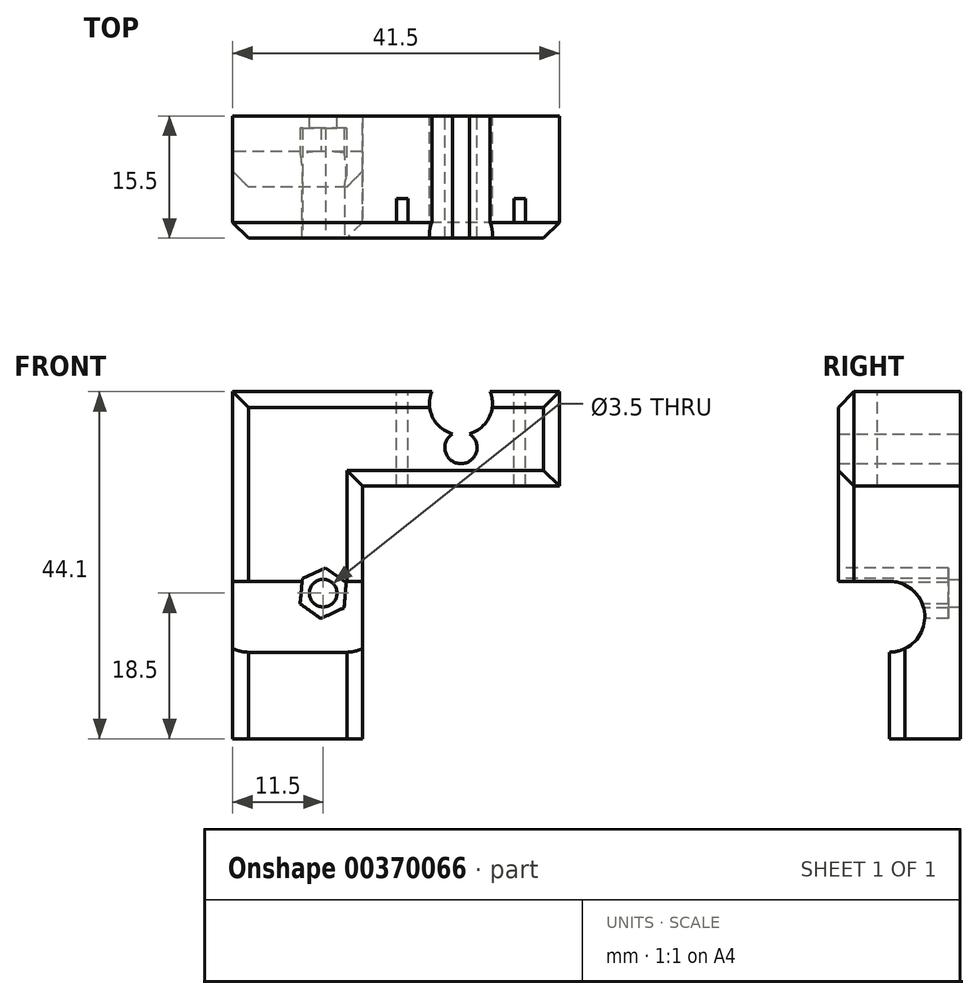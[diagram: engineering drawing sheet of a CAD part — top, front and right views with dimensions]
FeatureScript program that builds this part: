
annotation { "Feature Type Name" : "Feature", "Feature Type Description" : "" }
export const myFeature = defineFeature(function(context is Context, id is Id, definition is map)
    precondition{}
    {
        {
            var Q0;
            Q0=qCreatedBy(makeId("Front.planeOp"),FACE);
            var sketch = newSketch(context, id + "F0", { "sketchPlane" : qUnion([Q0])});
            skLineSegment(sketch, "E0.right", {"start": v(16.5, 21.37) * mm, "end": v(16.5, 38.5) * mm});
            skPoint(sketch, "E1.centerSnap0", {"position": v(8.25, 38.5) * mm});
            skLineSegment(sketch, "E2.trimOffspring", {"start": v(10.09, 38.5) * mm, "end": v(10.09, 38.5) * mm});
            skLineSegment(sketch, "E3", {"start": v(0, 38.5) * mm, "end": v(0, 21.37) * mm});
            skPoint(sketch, "E4.start.orphan", {"position": v(8.25, 33.37) * mm});
            skPoint(sketch, "E5.center.orphan", {"position": v(8.25, 37) * mm});
            skPoint(sketch, "E6.end.orphan", {"position": v(8.25, 21.37) * mm});
            skLineSegment(sketch, "E7", {"start": v(0, 38.5) * mm, "end": v(4.54, 38.5) * mm});
            skArc(sketch, "E8", {"start": v(4.54, 38.5) * mm, "mid": v(4.65, 35.25) * mm, "end": v(7.13, 33.16) * mm});
            skLineSegment(sketch, "E9.trimOffspring", {"start": v(11.96, 38.5) * mm, "end": v(16.5, 38.5) * mm});
            skArc(sketch, "E10", {"start": v(7.13, 33.16) * mm, "mid": v(8.25, 29.4) * mm, "end": v(9.37, 33.16) * mm});
            skArc(sketch, "E11.trimOffspring", {"start": v(9.37, 33.16) * mm, "mid": v(11.85, 35.25) * mm, "end": v(11.96, 38.5) * mm});
            skLineSegment(sketch, "E12", {"start": v(8.25, 21) * mm, "end": v(16.5, 21) * mm});
            skLineSegment(sketch, "E13", {"start": v(16.5, 21) * mm, "end": v(16.5, 21.37) * mm});
            skLineSegment(sketch, "E14", {"start": v(8.25, 21) * mm, "end": v(0, 21) * mm});
            skLineSegment(sketch, "E15", {"start": v(0, 21) * mm, "end": v(0, 21.37) * mm});
            skSolve(sketch);
        }
        {
            var Q0;
            Q0 = qSketchRegion(id + "F0", true);
            extrude(context, id + "F1", {"entities" : qUnion([Q0]), "depth" : 17.5 * mm});
        }
        {
            var Q0;
            Q0=makeQuery(id+"F1.opExtrude","CAP_FACE",FACE,{"disambiguationData":[OSD([sQuery(id+"F0.wireOp",EDGE,"E0.right"),sQuery(id+"F0.wireOp",EDGE,"E3"),sQuery(id+"F0.wireOp",EDGE,"E7"),sQuery(id+"F0.wireOp",EDGE,"E8"),sQuery(id+"F0.wireOp",EDGE,"E9.trimOffspring"),sQuery(id+"F0.wireOp",EDGE,"E10"),sQuery(id+"F0.wireOp",EDGE,"E11.trimOffspring"),sQuery(id+"F0.wireOp",EDGE,"E12"),sQuery(id+"F0.wireOp",EDGE,"E13"),sQuery(id+"F0.wireOp",EDGE,"E14"),sQuery(id+"F0.wireOp",EDGE,"E15")])],"isStart":true});
            var sketch = newSketch(context, id + "F2", { "sketchPlane" : qUnion([Q0])});
            skLineSegment(sketch, "E16.bottom", {"start": v(-16.5, 21) * mm, "end": v(0, 21) * mm});
            skLineSegment(sketch, "E16.top", {"start": v(-16.5, 1) * mm, "end": v(0, 1) * mm});
            skLineSegment(sketch, "E16.left", {"start": v(-16.5, 21) * mm, "end": v(-16.5, 1) * mm});
            skLineSegment(sketch, "E16.right", {"start": v(0, 21) * mm, "end": v(0, 1) * mm});
            skSolve(sketch);
        }
        {
            var Q0;
            Q0=makeQuery(id+"F2.imprint","IMPRINT",FACE,{"disambiguationData":[TD([[makeQuery(id+"F2.imprint","IMPRINT",EDGE,{"derivedFrom":sQuery(id+"F2.wireOp",EDGE,"E16.bottom")}),-1.0]])]});
            extrude(context, id + "F3", {"entities" : qUnion([Q0]), "operationType" : NewBodyOperationType.ADD, "oppositeDirection" : true, "depth" : 11 * mm});
        }
        {
            var Q0;
            Q0=makeQuery(id+"F3.boolean.opBoolean","MERGE",FACE,{"derivedFrom":[makeQuery(id+"F1.opExtrude","CAP_FACE",FACE,{"disambiguationData":[OSD([sQuery(id+"F0.wireOp",EDGE,"E0.right"),sQuery(id+"F0.wireOp",EDGE,"E3"),sQuery(id+"F0.wireOp",EDGE,"E7"),sQuery(id+"F0.wireOp",EDGE,"E8"),sQuery(id+"F0.wireOp",EDGE,"E9.trimOffspring"),sQuery(id+"F0.wireOp",EDGE,"E10"),sQuery(id+"F0.wireOp",EDGE,"E11.trimOffspring"),sQuery(id+"F0.wireOp",EDGE,"E12"),sQuery(id+"F0.wireOp",EDGE,"E13"),sQuery(id+"F0.wireOp",EDGE,"E14"),sQuery(id+"F0.wireOp",EDGE,"E15")])],"isStart":true}),makeQuery(id+"F3.opExtrude","CAP_FACE",FACE,{"disambiguationData":[OSD([sQuery(id+"F2.wireOp",EDGE,"E16.bottom"),sQuery(id+"F2.wireOp",EDGE,"E16.top"),sQuery(id+"F2.wireOp",EDGE,"E16.left"),sQuery(id+"F2.wireOp",EDGE,"E16.right")])],"isStart":true})]});
            var sketch = newSketch(context, id + "F4", { "sketchPlane" : qUnion([Q0])});
            skPoint(sketch, "E17.endSnap0", {"position": v(-8.25, 29.4) * mm});
            skCircle(sketch, "E18", {"center": v(-11.5, 19.5) * mm, "radius": 1.75 * mm});
            skPoint(sketch, "E19.orphan", {"position": v(-16.5, 19.5) * mm});
            skPoint(sketch, "E20.end.orphan", {"position": v(-8.25, 19.5) * mm});
            skSolve(sketch);
        }
        {
            var Q0;
            Q0=makeQuery(id+"F3.boolean.opBoolean","MERGE",FACE,{"derivedFrom":[makeQuery(id+"F1.opExtrude","SWEPT_FACE",FACE,{"disambiguationData":[OSD([sQuery(id+"F0.wireOp",EDGE,"E3"),sQuery(id+"F0.wireOp",EDGE,"E15")])]}),makeQuery(id+"F3.opExtrude","SWEPT_FACE",FACE,{"disambiguationData":[OSD([sQuery(id+"F2.wireOp",EDGE,"E16.right")])]})]});
            var sketch = newSketch(context, id + "F5", { "sketchPlane" : qUnion([Q0])});
            skLineSegment(sketch, "E21", {"start": v(11, 21) * mm, "end": v(11, 16.5) * mm});
            skArc(sketch, "E22", {"start": v(11, 21) * mm, "mid": v(6.5, 16.5) * mm, "end": v(11, 12) * mm});
            skLineSegment(sketch, "E23", {"start": v(11, 16.5) * mm, "end": v(11, 12) * mm});
            skPoint(sketch, "E24.orphan", {"position": v(11, 11) * mm});
            skSolve(sketch);
        }
        {
            var Q0;
            Q0 = qSketchRegion(id + "F4", true);
            extrude(context, id + "F6", {"entities" : qUnion([Q0]), "operationType" : NewBodyOperationType.REMOVE, "oppositeDirection" : true, "depth" : 22.5 * mm});
        }
        {
            var Q0;
            Q0=makeQuery(id+"F3.opExtrude","CAP_FACE",FACE,{"disambiguationData":[OSD([sQuery(id+"F2.wireOp",EDGE,"E16.bottom"),sQuery(id+"F2.wireOp",EDGE,"E16.top"),sQuery(id+"F2.wireOp",EDGE,"E16.left"),sQuery(id+"F2.wireOp",EDGE,"E16.right")])],"isStart":false});
            var sketch = newSketch(context, id + "F7", { "sketchPlane" : qUnion([Q0])});
            skCircle(sketch, "E25.cCircle", {"center": v(11.5, 19.5) * mm, "radius": 2.8 * mm, "construction": true});
            skLineSegment(sketch, "E25.0", {"start": v(14.43, 20.86) * mm, "end": v(14.14, 17.64) * mm});
            skLineSegment(sketch, "E25.1", {"start": v(14.14, 17.64) * mm, "end": v(11.2, 16.28) * mm});
            skLineSegment(sketch, "E25.2", {"start": v(11.2, 16.28) * mm, "end": v(8.57, 18.14) * mm});
            skLineSegment(sketch, "E25.3", {"start": v(8.57, 18.14) * mm, "end": v(8.86, 21.36) * mm});
            skLineSegment(sketch, "E25.4", {"start": v(8.86, 21.36) * mm, "end": v(11.8, 22.72) * mm});
            skLineSegment(sketch, "E25.5", {"start": v(11.8, 22.72) * mm, "end": v(14.43, 20.86) * mm});
            skPoint(sketch, "E25.0.midPoint", {"position": v(14.29, 19.25) * mm});
            skSolve(sketch);
        }
        {
            var Q0;
            Q0 = qSketchRegion(id + "F7", true);
            extrude(context, id + "F8", {"entities" : qUnion([Q0]), "operationType" : NewBodyOperationType.REMOVE, "oppositeDirection" : true, "depth" : 7.5 * mm});
        }
        {
            var Q0;
            Q0 = qSketchRegion(id + "F7", true);
            extrude(context, id + "F9", {"entities" : qUnion([Q0]), "operationType" : NewBodyOperationType.REMOVE, "depth" : 13.1 * mm});
        }
        {
            var Q0;
            Q0 = qSketchRegion(id + "F5", true);
            extrude(context, id + "F10", {"entities" : qUnion([Q0]), "operationType" : NewBodyOperationType.REMOVE, "oppositeDirection" : true, "depth" : 24.9 * mm});
        }
        {
            var Q0;
            Q0=makeQuery(id+"F3.boolean.opBoolean","MERGE",FACE,{"derivedFrom":[makeQuery(id+"F1.opExtrude","CAP_FACE",FACE,{"disambiguationData":[OSD([sQuery(id+"F0.wireOp",EDGE,"E0.right"),sQuery(id+"F0.wireOp",EDGE,"E3"),sQuery(id+"F0.wireOp",EDGE,"E7"),sQuery(id+"F0.wireOp",EDGE,"E8"),sQuery(id+"F0.wireOp",EDGE,"E9.trimOffspring"),sQuery(id+"F0.wireOp",EDGE,"E10"),sQuery(id+"F0.wireOp",EDGE,"E11.trimOffspring"),sQuery(id+"F0.wireOp",EDGE,"E12"),sQuery(id+"F0.wireOp",EDGE,"E13"),sQuery(id+"F0.wireOp",EDGE,"E14"),sQuery(id+"F0.wireOp",EDGE,"E15")])],"isStart":true}),makeQuery(id+"F3.opExtrude","CAP_FACE",FACE,{"disambiguationData":[OSD([sQuery(id+"F2.wireOp",EDGE,"E16.bottom"),sQuery(id+"F2.wireOp",EDGE,"E16.top"),sQuery(id+"F2.wireOp",EDGE,"E16.left"),sQuery(id+"F2.wireOp",EDGE,"E16.right")])],"isStart":true})]});
            var sketch = newSketch(context, id + "F11", { "sketchPlane" : qUnion([Q0])});
            skLineSegment(sketch, "E26", {"start": v(-16.5, 38.5) * mm, "end": v(-16.5, 1) * mm});
            skLineSegment(sketch, "E27", {"start": v(-16.5, 1) * mm, "end": v(0, 1) * mm});
            skLineSegment(sketch, "E28", {"start": v(0, 1) * mm, "end": v(0, 38.5) * mm});
            skLineSegment(sketch, "E29", {"start": v(0, 38.5) * mm, "end": v(-4.54, 38.5) * mm});
            skLineSegment(sketch, "E30", {"start": v(-11.96, 38.5) * mm, "end": v(-16.5, 38.5) * mm});
            skArc(sketch, "E31", {"start": v(-11.96, 38.5) * mm, "mid": v(-11.85, 35.25) * mm, "end": v(-9.37, 33.16) * mm});
            skArc(sketch, "E32", {"start": v(-9.37, 33.16) * mm, "mid": v(-8.25, 29.4) * mm, "end": v(-7.13, 33.16) * mm});
            skArc(sketch, "E33.trimOffspring", {"start": v(-7.13, 33.16) * mm, "mid": v(-4.65, 35.25) * mm, "end": v(-4.54, 38.5) * mm});
            skSolve(sketch);
        }
        {
            var Q0;
            Q0=makeQuery(id+"F11.imprint","IMPRINT",FACE,{"disambiguationData":[TD([[makeQuery(id+"F11.imprint","IMPRINT",EDGE,{"derivedFrom":sQuery(id+"F11.wireOp",EDGE,"E26")}),-1.0]])]});
            extrude(context, id + "F12", {"entities" : qUnion([Q0]), "operationType" : NewBodyOperationType.REMOVE, "oppositeDirection" : true, "depth" : 2 * mm});
        }
        {
            var Q0;
            Q0=makeQuery(id+"F3.boolean.opBoolean","MERGE",FACE,{"derivedFrom":[makeQuery(id+"F1.opExtrude","SWEPT_FACE",FACE,{"disambiguationData":[OSD([sQuery(id+"F0.wireOp",EDGE,"E0.right"),sQuery(id+"F0.wireOp",EDGE,"E13")])]}),makeQuery(id+"F3.opExtrude","SWEPT_FACE",FACE,{"disambiguationData":[OSD([sQuery(id+"F2.wireOp",EDGE,"E16.left")])]})]});
            var sketch = newSketch(context, id + "F13", { "sketchPlane" : qUnion([Q0])});
            skLineSegment(sketch, "E34.top", {"start": v(-2, 33.1) * mm, "end": v(-17.5, 33.1) * mm});
            skLineSegment(sketch, "E34.left", {"start": v(-2, 38.5) * mm, "end": v(-2, 33.1) * mm});
            skLineSegment(sketch, "E34.right", {"start": v(-17.5, 38.5) * mm, "end": v(-17.5, 33.1) * mm});
            skLineSegment(sketch, "E35.top", {"start": v(-2, 45.1) * mm, "end": v(-17.5, 45.1) * mm});
            skLineSegment(sketch, "E35.left", {"start": v(-2, 38.5) * mm, "end": v(-2, 45.1) * mm});
            skLineSegment(sketch, "E35.right", {"start": v(-17.5, 38.5) * mm, "end": v(-17.5, 45.1) * mm});
            skSolve(sketch);
        }
        {
            var Q0;
            Q0=makeQuery(id+"F13.imprint","IMPRINT",FACE,{"disambiguationData":[TD([[makeQuery(id+"F13.imprint","IMPRINT",EDGE,{"derivedFrom":sQuery(id+"F13.wireOp",EDGE,"E35.top")}),1.0]])]});
            var Q1;
            Q1=makeQuery(id+"F13.imprint","IMPRINT",FACE,{"disambiguationData":[TD([[makeQuery(id+"F13.imprint","IMPRINT",EDGE,{"derivedFrom":sQuery(id+"F13.wireOp",EDGE,"E34.top")}),-1.0]])]});
            extrude(context, id + "F14", {"entities" : qUnion([Q0, Q1]), "operationType" : NewBodyOperationType.ADD, "depth" : 25 * mm});
        }
        {
            var Q0;
            Q0=makeQuery(id+"F14.opExtrude","CAP_FACE",FACE,{"disambiguationData":[OSD([sQuery(id+"F13.wireOp",EDGE,"E34.top"),sQuery(id+"F13.wireOp",EDGE,"E34.left"),sQuery(id+"F13.wireOp",EDGE,"E34.right"),sQuery(id+"F13.wireOp",EDGE,"E35.top"),sQuery(id+"F13.wireOp",EDGE,"E35.left"),sQuery(id+"F13.wireOp",EDGE,"E35.right")])],"isStart":true});
            extrude(context, id + "F15", {"entities" : qUnion([Q0]), "operationType" : NewBodyOperationType.ADD, "depth" : 16.5 * mm});
        }
        {
            var Q0;
            {var subQ0=sQuery(id+"F13.wireOp",EDGE,"E35.left");var subQ1=sQuery(id+"F13.wireOp",EDGE,"E34.left");Q0=makeQuery(id+"F15.boolean.opBoolean","MERGE",FACE,{"derivedFrom":[makeQuery(id+"F14.boolean.opBoolean","MERGE",FACE,{"derivedFrom":[makeQuery(id+"F12.boolean.opBoolean","COPY",FACE,{"derivedFrom":makeQuery(id+"F12.opExtrude","CAP_FACE",FACE,{"disambiguationData":[OSD([sQuery(id+"F4.wireOp",EDGE,"E18"),sQuery(id+"F11.wireOp",EDGE,"E26"),sQuery(id+"F11.wireOp",EDGE,"E27"),sQuery(id+"F11.wireOp",EDGE,"E28"),sQuery(id+"F11.wireOp",EDGE,"E29"),sQuery(id+"F11.wireOp",EDGE,"E30"),sQuery(id+"F11.wireOp",EDGE,"E31"),sQuery(id+"F11.wireOp",EDGE,"E32"),sQuery(id+"F11.wireOp",EDGE,"E33.trimOffspring")])],"isStart":false})}),makeQuery(id+"F14.opExtrude","SWEPT_FACE",FACE,{"disambiguationData":[OSD([subQ1,subQ0])]})]}),makeQuery(id+"F15.opExtrude","SWEPT_FACE",FACE,{"disambiguationData":[OSD([subQ1,subQ0])]})]});}
            var sketch = newSketch(context, id + "F16", { "sketchPlane" : qUnion([Q0])});
            skPoint(sketch, "E36.endSnap0", {"position": v(-29, 45.1) * mm});
            skArc(sketch, "E37", {"start": v(-27.93, 39.74) * mm, "mid": v(-25.4, 41.83) * mm, "end": v(-25.3, 45.1) * mm});
            skPoint(sketch, "E36.start.orphan", {"position": v(-29, 45.1) * mm});
            skArc(sketch, "E38", {"start": v(-30.07, 39.74) * mm, "mid": v(-29, 35.94) * mm, "end": v(-27.93, 39.74) * mm});
            skArc(sketch, "E39.trimOffspring", {"start": v(-32.7, 45.1) * mm, "mid": v(-32.6, 41.83) * mm, "end": v(-30.07, 39.74) * mm});
            skPoint(sketch, "E40.trimOffspring.end.orphan", {"position": v(-41.5, 45.1) * mm});
            skPoint(sketch, "E41.start.orphan", {"position": v(-16.5, 45.1) * mm});
            skLineSegment(sketch, "E42", {"start": v(-32.7, 45.1) * mm, "end": v(-25.3, 45.1) * mm});
            skSolve(sketch);
        }
        {
            var Q0;
            Q0 = qSketchRegion(id + "F16", true);
            extrude(context, id + "F17", {"entities" : qUnion([Q0]), "operationType" : NewBodyOperationType.REMOVE, "oppositeDirection" : true, "depth" : 25 * mm});
        }
        {
            var Q0;
            {var subQ6=sQuery(id+"F13.wireOp",EDGE,"E35.top");Q0=makeQuery(id+"F17.boolean.opBoolean","SPLIT",FACE,{"disambiguationData":[TD([makeQuery(id+"F3.opExtrude","SWEPT_FACE",FACE,{"disambiguationData":[OSD([sQuery(id+"F2.wireOp",EDGE,"E16.right")])]})])],"derivedFrom":makeQuery(id+"F15.boolean.opBoolean","MERGE",FACE,{"derivedFrom":[makeQuery(id+"F14.opExtrude","SWEPT_FACE",FACE,{"disambiguationData":[OSD([subQ6])]}),makeQuery(id+"F15.opExtrude","SWEPT_FACE",FACE,{"disambiguationData":[OSD([subQ6])]})]})});}
            var sketch = newSketch(context, id + "F18", { "sketchPlane" : qUnion([Q0])});
            skLineSegment(sketch, "E43.bottom", {"start": v(20.8, -12.5) * mm, "end": v(22.3, -12.5) * mm});
            skLineSegment(sketch, "E43.top", {"start": v(20.8, -15.5) * mm, "end": v(22.3, -15.5) * mm});
            skLineSegment(sketch, "E43.left", {"start": v(20.8, -12.5) * mm, "end": v(20.8, -15.5) * mm});
            skLineSegment(sketch, "E43.right", {"start": v(22.3, -12.5) * mm, "end": v(22.3, -15.5) * mm});
            skLineSegment(sketch, "E44.bottom", {"start": v(35.7, -12.5) * mm, "end": v(37.2, -12.5) * mm});
            skLineSegment(sketch, "E44.top", {"start": v(35.7, -15.5) * mm, "end": v(37.2, -15.5) * mm});
            skLineSegment(sketch, "E44.left", {"start": v(35.7, -12.5) * mm, "end": v(35.7, -15.5) * mm});
            skLineSegment(sketch, "E44.right", {"start": v(37.2, -12.5) * mm, "end": v(37.2, -15.5) * mm});
            skSolve(sketch);
        }
        {
            var Q0;
            Q0 = qSketchRegion(id + "F18", true);
            extrude(context, id + "F19", {"entities" : qUnion([Q0]), "operationType" : NewBodyOperationType.REMOVE, "oppositeDirection" : true, "depth" : 25 * mm});
        }
        {
            var Q0;
            {var subQ0=sQuery(id+"F13.wireOp",EDGE,"E35.right");var subQ1=sQuery(id+"F13.wireOp",EDGE,"E34.right");Q0=makeQuery(id+"F15.boolean.opBoolean","MERGE",FACE,{"derivedFrom":[makeQuery(id+"F14.boolean.opBoolean","MERGE",FACE,{"derivedFrom":[makeQuery(id+"F1.opExtrude","CAP_FACE",FACE,{"disambiguationData":[OSD([sQuery(id+"F0.wireOp",EDGE,"E0.right"),sQuery(id+"F0.wireOp",EDGE,"E3"),sQuery(id+"F0.wireOp",EDGE,"E7"),sQuery(id+"F0.wireOp",EDGE,"E8"),sQuery(id+"F0.wireOp",EDGE,"E9.trimOffspring"),sQuery(id+"F0.wireOp",EDGE,"E10"),sQuery(id+"F0.wireOp",EDGE,"E11.trimOffspring"),sQuery(id+"F0.wireOp",EDGE,"E12"),sQuery(id+"F0.wireOp",EDGE,"E13"),sQuery(id+"F0.wireOp",EDGE,"E14"),sQuery(id+"F0.wireOp",EDGE,"E15")])],"isStart":false}),makeQuery(id+"F14.opExtrude","SWEPT_FACE",FACE,{"disambiguationData":[OSD([subQ1,subQ0])]})]}),makeQuery(id+"F15.opExtrude","SWEPT_FACE",FACE,{"disambiguationData":[OSD([subQ1,subQ0])]})]});}
            var sketch = newSketch(context, id + "F20", { "sketchPlane" : qUnion([Q0])});
            skPoint(sketch, "E45.1", {"position": v(8.25, 38.5) * mm});
            skLineSegment(sketch, "E45.2", {"start": v(10.09, 38.5) * mm, "end": v(10.09, 38.5) * mm});
            skLineSegment(sketch, "E45.3", {"start": v(10.09, 38.5) * mm, "end": v(10.09, 38.5) * mm});
            skLineSegment(sketch, "E45.4", {"start": v(10.09, 38.5) * mm, "end": v(10.09, 38.5) * mm});
            skPoint(sketch, "E45.6", {"position": v(8.25, 33.37) * mm});
            skPoint(sketch, "E45.7", {"position": v(8.25, 37) * mm});
            skPoint(sketch, "E45.8", {"position": v(8.25, 21.37) * mm});
            skArc(sketch, "E45.10", {"start": v(4.54, 38.5) * mm, "mid": v(4.65, 35.25) * mm, "end": v(7.13, 33.16) * mm});
            skLineSegment(sketch, "E45.11", {"start": v(10.09, 38.5) * mm, "end": v(10.09, 38.5) * mm});
            skArc(sketch, "E45.13", {"start": v(7.13, 33.16) * mm, "mid": v(8.25, 29.4) * mm, "end": v(9.37, 33.16) * mm});
            skArc(sketch, "E45.14", {"start": v(9.37, 33.16) * mm, "mid": v(11.85, 35.25) * mm, "end": v(11.96, 38.5) * mm});
            skPoint(sketch, "E45.5.end.orphan", {"position": v(0, 21.37) * mm});
            skPoint(sketch, "E45.5.start.orphan", {"position": v(0, 38.5) * mm});
            skPoint(sketch, "E45.9.end.orphan", {"position": v(4.54, 38.5) * mm});
            skPoint(sketch, "E45.9.start.orphan", {"position": v(0, 38.5) * mm});
            skPoint(sketch, "E45.12.end.orphan", {"position": v(16.5, 38.5) * mm});
            skPoint(sketch, "E45.12.start.orphan", {"position": v(11.96, 38.5) * mm});
            skPoint(sketch, "E45.0.end.orphan", {"position": v(16.5, 38.5) * mm});
            skPoint(sketch, "E45.0.start.orphan", {"position": v(16.5, 21.37) * mm});
            skPoint(sketch, "E45.17.end.orphan", {"position": v(0, 21) * mm});
            skPoint(sketch, "E45.17.start.orphan", {"position": v(8.25, 21) * mm});
            skPoint(sketch, "E45.15.end.orphan", {"position": v(16.5, 21) * mm});
            skPoint(sketch, "E45.15.start.orphan", {"position": v(8.25, 21) * mm});
            skPoint(sketch, "E45.16.end.orphan", {"position": v(16.5, 21.37) * mm});
            skPoint(sketch, "E45.16.start.orphan", {"position": v(16.5, 21) * mm});
            skPoint(sketch, "E45.18.end.orphan", {"position": v(0, 21.37) * mm});
            skPoint(sketch, "E45.18.start.orphan", {"position": v(0, 21) * mm});
            skLineSegment(sketch, "E46", {"start": v(4.54, 38.5) * mm, "end": v(11.96, 38.5) * mm});
            skSolve(sketch);
        }
        {
            var Q0;
            {var subQ1=sQuery(id+"F20.wireOp",EDGE,"E45.10");Q0=makeQuery(id+"F20.imprint","IMPRINT",FACE,{"disambiguationData":[TD([[makeQuery(id+"F20.imprint","IMPRINT",EDGE,{"derivedFrom":subQ1}),1.0]])]});}
            extrude(context, id + "F21", {"entities" : qUnion([Q0]), "operationType" : NewBodyOperationType.ADD, "oppositeDirection" : true, "depth" : 15.5 * mm});
        }
        {
            var Q0;
            Q0=makeQuery(id+"F14.opExtrude","CAP_EDGE",EDGE,{"disambiguationData":[OSD([sQuery(id+"F13.wireOp",EDGE,"E34.right"),sQuery(id+"F13.wireOp",EDGE,"E35.right")])],"isStart":false});
            var Q1;
            Q1=makeQuery(id+"F15.boolean.opBoolean","MERGE",EDGE,{"derivedFrom":[makeQuery(id+"F1.opExtrude","CAP_EDGE",EDGE,{"disambiguationData":[OSD([sQuery(id+"F0.wireOp",EDGE,"E3"),sQuery(id+"F0.wireOp",EDGE,"E15")])],"isStart":false}),makeQuery(id+"F15.opExtrude","CAP_EDGE",EDGE,{"disambiguationData":[OSD([sQuery(id+"F13.wireOp",EDGE,"E34.right"),sQuery(id+"F13.wireOp",EDGE,"E35.right")])],"isStart":false})]});
            var Q2;
            Q2=makeQuery(id+"F1.opExtrude","CAP_EDGE",EDGE,{"disambiguationData":[OSD([sQuery(id+"F0.wireOp",EDGE,"E0.right"),sQuery(id+"F0.wireOp",EDGE,"E13")])],"isStart":false});
            var Q3;
            Q3=makeQuery(id+"F14.opExtrude","SWEPT_EDGE",EDGE,{"disambiguationData":[OSD([sQuery(id+"F0.wireOp",EDGE,"E0.right"),sQuery(id+"F0.wireOp",EDGE,"E13"),sQuery(id+"F13.wireOp",EDGE,"E34.top"),sQuery(id+"F13.wireOp",EDGE,"E34.right")])]});
            var Q4;
            {var subQ0=sQuery(id+"F13.wireOp",EDGE,"E35.right");var subQ2=sQuery(id+"F13.wireOp",EDGE,"E35.top");Q4=makeQuery(id+"F17.boolean.opBoolean","SPLIT",EDGE,{"disambiguationData":[TD([makeQuery(id+"F3.opExtrude","SWEPT_FACE",FACE,{"disambiguationData":[OSD([sQuery(id+"F2.wireOp",EDGE,"E16.right")])]})])],"derivedFrom":makeQuery(id+"F15.boolean.opBoolean","MERGE",EDGE,{"derivedFrom":[makeQuery(id+"F14.opExtrude","SWEPT_EDGE",EDGE,{"disambiguationData":[OSD([subQ2,subQ0])]}),makeQuery(id+"F15.opExtrude","SWEPT_EDGE",EDGE,{"disambiguationData":[OSD([subQ2,subQ0])]})]})});}
            var Q5;
            {var subQ0=sQuery(id+"F13.wireOp",EDGE,"E35.top");var subQ1=sQuery(id+"F13.wireOp",EDGE,"E35.right");Q5=makeQuery(id+"F17.boolean.opBoolean","SPLIT",EDGE,{"disambiguationData":[TD([makeQuery(id+"F17.opExtrude","SWEPT_FACE",FACE,{"disambiguationData":[OSD([sQuery(id+"F16.wireOp",EDGE,"E39.trimOffspring")])]})])],"derivedFrom":makeQuery(id+"F15.boolean.opBoolean","MERGE",EDGE,{"derivedFrom":[makeQuery(id+"F14.opExtrude","SWEPT_EDGE",EDGE,{"disambiguationData":[OSD([subQ0,subQ1])]}),makeQuery(id+"F15.opExtrude","SWEPT_EDGE",EDGE,{"disambiguationData":[OSD([subQ0,subQ1])]})]})});}
            chamfer(context, id + "F22", {"entities" : qUnion([Q0, Q1, Q2, Q3, Q4, Q5]), "width" : 2 * mm, "tangentPropagation" : true});
        }
        {
            var Q0;
            Q0=makeQuery(id+"F3.opExtrude","CAP_EDGE",EDGE,{"disambiguationData":[OSD([sQuery(id+"F2.wireOp",EDGE,"E16.right")])],"isStart":false});
            var Q1;
            Q1=makeQuery(id+"F3.opExtrude","CAP_EDGE",EDGE,{"disambiguationData":[OSD([sQuery(id+"F2.wireOp",EDGE,"E16.left")])],"isStart":false});
            chamfer(context, id + "F23", {"entities" : qUnion([Q0, Q1]), "width" : 2 * mm, "tangentPropagation" : true});
        }
    });
